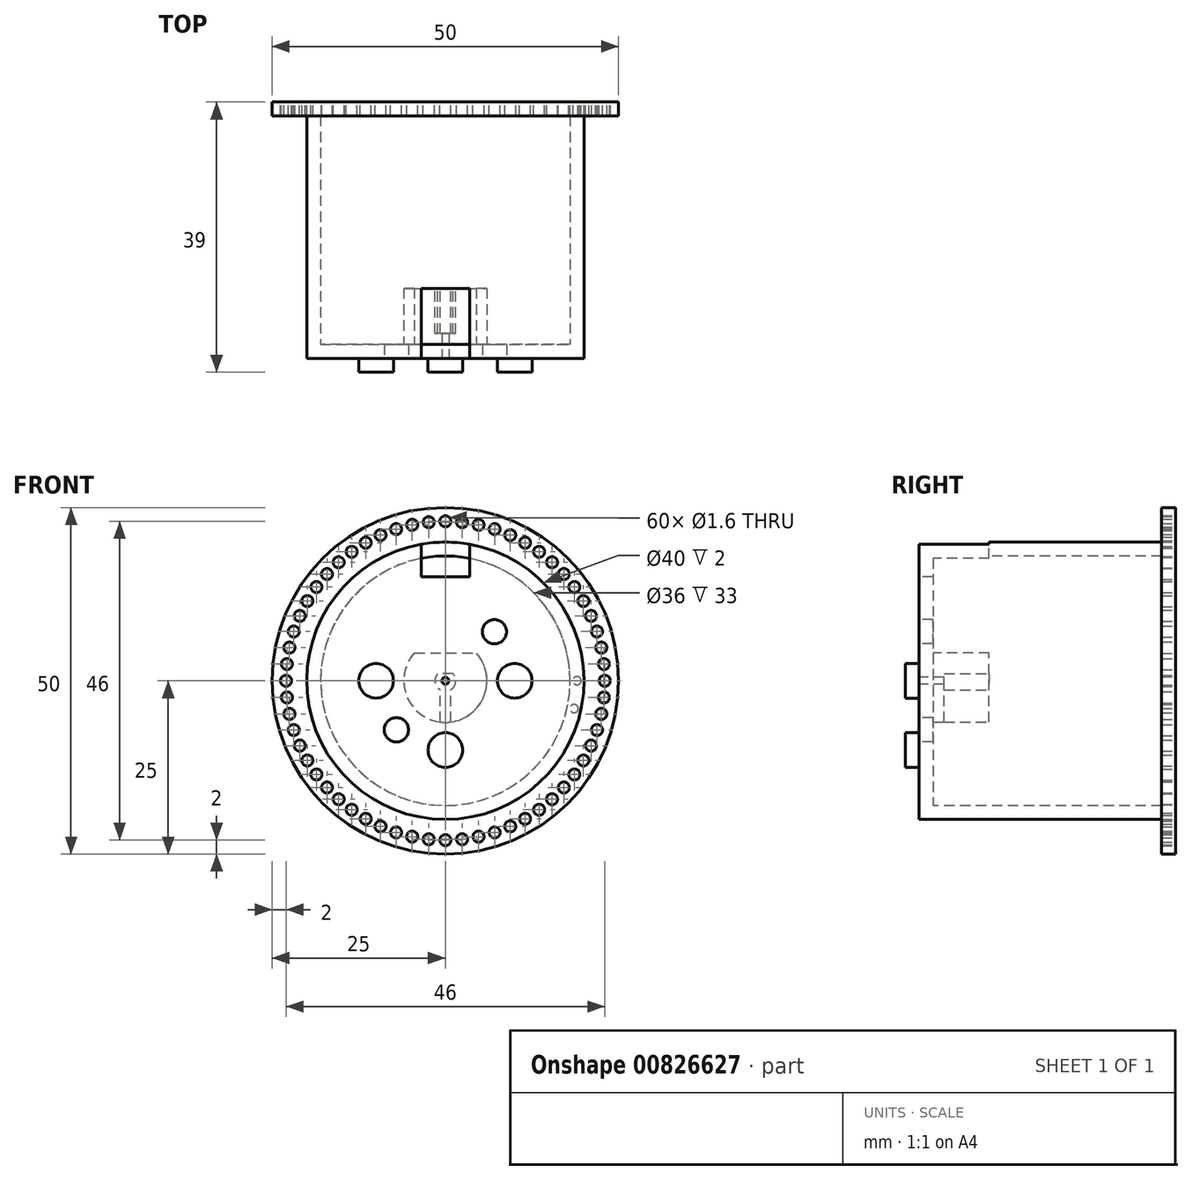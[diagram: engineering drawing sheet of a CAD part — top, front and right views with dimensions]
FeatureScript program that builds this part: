
annotation { "Feature Type Name" : "Feature", "Feature Type Description" : "" }
export const myFeature = defineFeature(function(context is Context, id is Id, definition is map)
    precondition{}
    {
        {
            var Q0;
            Q0=qCreatedBy(makeId("Front.planeOp"),FACE);
            var sketch = newSketch(context, id + "F0", { "sketchPlane" : qUnion([Q0])});
            skCircle(sketch, "E0", {"center": v(0, 0) * mm, "radius": 20 * mm});
            skCircle(sketch, "E1", {"center": v(0, 0) * mm, "radius": 6 * mm});
            skLineSegment(sketch, "E2", {"start": v(0, 0) * mm, "end": v(0, 20) * mm, "construction": true});
            skLineSegment(sketch, "E3.bottom", {"start": v(-3.5, 20) * mm, "end": v(3.5, 20) * mm});
            skLineSegment(sketch, "E3.top", {"start": v(-3.5, 15) * mm, "end": v(3.5, 15) * mm});
            skLineSegment(sketch, "E3.left", {"start": v(-3.5, 20) * mm, "end": v(-3.5, 15) * mm});
            skLineSegment(sketch, "E3.right", {"start": v(3.5, 20) * mm, "end": v(3.5, 15) * mm});
            skPoint(sketch, "E4", {"position": v(0, 15) * mm});
            skLineSegment(sketch, "E5", {"start": v(0, -20) * mm, "end": v(0, 0) * mm, "construction": true});
            skLineSegment(sketch, "E6", {"start": v(0, 0) * mm, "end": v(-20, 0) * mm, "construction": true});
            skLineSegment(sketch, "E7", {"start": v(0, 0) * mm, "end": v(20, 0) * mm, "construction": true});
            skPoint(sketch, "E8", {"position": v(-10, 0) * mm});
            skPoint(sketch, "E9", {"position": v(0, -10) * mm});
            skPoint(sketch, "E10", {"position": v(10, 0) * mm});
            skPoint(sketch, "E11", {"position": v(0, 10) * mm});
            skCircle(sketch, "E12", {"center": v(-10, 0) * mm, "radius": 2.5 * mm});
            skCircle(sketch, "E13", {"center": v(10, 0) * mm, "radius": 2.5 * mm});
            skCircle(sketch, "E14", {"center": v(0, -10) * mm, "radius": 2.5 * mm});
            skLineSegment(sketch, "E15", {"start": v(0, 0) * mm, "end": v(-20, -20) * mm, "construction": true});
            skLineSegment(sketch, "E16", {"start": v(0, 0) * mm, "end": v(20, 20) * mm, "construction": true});
            skLineSegment(sketch, "E17", {"start": v(0, 0) * mm, "end": v(20, -20) * mm, "construction": true});
            skLineSegment(sketch, "E18", {"start": v(0, 0) * mm, "end": v(-14.14, -14.14) * mm, "construction": true});
            skCircle(sketch, "E19", {"center": v(-7.07, -7.07) * mm, "radius": 1.75 * mm});
            skLineSegment(sketch, "E20", {"start": v(0, 0) * mm, "end": v(14.14, 14.14) * mm, "construction": true});
            skCircle(sketch, "E21", {"center": v(7.07, 7.07) * mm, "radius": 1.75 * mm});
            skLineSegment(sketch, "E22", {"start": v(-4.47, 4) * mm, "end": v(4.47, 4) * mm});
            skCircle(sketch, "E23", {"center": v(0, 0) * mm, "radius": 0.5 * mm});
            skSolve(sketch);
        }
        {
            var Q0;
            Q0=makeQuery(id+"F0.imprint","IMPRINT",FACE,{"disambiguationData":[TD([[makeQuery(id+"F0.imprint","IMPRINT",EDGE,{"derivedFrom":sQuery(id+"F0.wireOp",EDGE,"E1")}),-1.0]])]});
            var Q1;
            Q1=makeQuery(id+"F0.imprint","IMPRINT",FACE,{"disambiguationData":[TD([[makeQuery(id+"F0.imprint","IMPRINT",EDGE,{"derivedFrom":sQuery(id+"F0.wireOp",EDGE,"E1")}),1.0]])]});
            var Q2;
            {var subQ1=sQuery(id+"F0.wireOp",EDGE,"E3.top");Q2=makeQuery(id+"F0.imprint","IMPRINT",FACE,{"disambiguationData":[TD([[makeQuery(id+"F0.imprint","IMPRINT",EDGE,{"derivedFrom":subQ1}),1.0]])]});}
            var Q3;
            {var subQ0=sQuery(id+"F0.wireOp",EDGE,"Ytkhx9iy-BOv9-2ljm-Vuet-2ZozW4X65qVo.right");Q3=makeQuery(id+"F0.imprint","IMPRINT",FACE,{"disambiguationData":[TD([[makeQuery(id+"F0.imprint","IMPRINT",EDGE,{"derivedFrom":subQ0}),-1.0]])]});}
            var Q4;
            {var subQ0=sQuery(id+"F0.wireOp",EDGE,"KaZ6fn21-f6RE-yPpd-ZOH6-FnEf13cd3E14.left");Q4=makeQuery(id+"F0.imprint","IMPRINT",FACE,{"disambiguationData":[TD([[makeQuery(id+"F0.imprint","IMPRINT",EDGE,{"derivedFrom":subQ0}),1.0]])]});}
            var Q5;
            {var subQ1=sQuery(id+"F0.wireOp",EDGE,"QGJammbx-tseF-7Ff8-FYSq-d8eIJjrRkEd8.bottom");Q5=makeQuery(id+"F0.imprint","IMPRINT",FACE,{"disambiguationData":[TD([[makeQuery(id+"F0.imprint","IMPRINT",EDGE,{"derivedFrom":subQ1}),-1.0]])]});}
            var Q6;
            Q6=makeQuery(id+"F0.imprint","IMPRINT",FACE,{"disambiguationData":[TD([[makeQuery(id+"F0.imprint","IMPRINT",EDGE,{"derivedFrom":sQuery(id+"F0.wireOp",EDGE,"E12")}),1.0]])]});
            var Q7;
            Q7=makeQuery(id+"F0.imprint","IMPRINT",FACE,{"disambiguationData":[TD([[makeQuery(id+"F0.imprint","IMPRINT",EDGE,{"derivedFrom":sQuery(id+"F0.wireOp",EDGE,"E19")}),1.0]])]});
            var Q8;
            Q8=makeQuery(id+"F0.imprint","IMPRINT",FACE,{"disambiguationData":[TD([[makeQuery(id+"F0.imprint","IMPRINT",EDGE,{"derivedFrom":sQuery(id+"F0.wireOp",EDGE,"E14")}),1.0]])]});
            var Q9;
            Q9=makeQuery(id+"F0.imprint","IMPRINT",FACE,{"disambiguationData":[TD([[makeQuery(id+"F0.imprint","IMPRINT",EDGE,{"derivedFrom":sQuery(id+"F0.wireOp",EDGE,"E13")}),1.0]])]});
            var Q10;
            Q10=makeQuery(id+"F0.imprint","IMPRINT",FACE,{"disambiguationData":[TD([[makeQuery(id+"F0.imprint","IMPRINT",EDGE,{"derivedFrom":sQuery(id+"F0.wireOp",EDGE,"E21")}),1.0]])]});
            var Q11;
            {var subQ0=sQuery(id+"F0.wireOp",EDGE,"E22");Q11=makeQuery(id+"F0.imprint","IMPRINT",FACE,{"disambiguationData":[TD([[makeQuery(id+"F0.imprint","IMPRINT",EDGE,{"derivedFrom":subQ0}),-1.0]])]});}
            var Q12;
            Q12=makeQuery(id+"F0.imprint","IMPRINT",FACE,{"disambiguationData":[TD([[makeQuery(id+"F0.imprint","IMPRINT",EDGE,{"derivedFrom":sQuery(id+"F0.wireOp",EDGE,"E23")}),1.0]])]});
            extrude(context, id + "F1", {"entities" : qUnion([Q0, Q1, Q2, Q3, Q4, Q5, Q6, Q7, Q8, Q9, Q10, Q11, Q12]), "oppositeDirection" : true, "depth" : 37 * mm});
        }
        {
            var Q0;
            Q0=makeQuery(id+"F1.opExtrude","CAP_FACE",FACE,{"disambiguationData":[OSD([sQuery(id+"F0.wireOp",EDGE,"E0"),sQuery(id+"F0.wireOp",EDGE,"E3.top"),sQuery(id+"F0.wireOp",EDGE,"E3.left"),sQuery(id+"F0.wireOp",EDGE,"E3.right")])],"isStart":false});
            var Q1;
            Q1=makeQuery(id+"F1.opExtrude","SWEPT_FACE",FACE,{"disambiguationData":[OSD([sQuery(id+"F0.wireOp",EDGE,"E19")])]});
            var Q2;
            Q2=makeQuery(id+"F1.opExtrude","SWEPT_FACE",FACE,{"disambiguationData":[OSD([sQuery(id+"F0.wireOp",EDGE,"E14")])]});
            var Q3;
            Q3=makeQuery(id+"F1.opExtrude","SWEPT_FACE",FACE,{"disambiguationData":[OSD([sQuery(id+"F0.wireOp",EDGE,"E21")])]});
            var Q4;
            Q4=makeQuery(id+"F1.opExtrude","SWEPT_FACE",FACE,{"disambiguationData":[OSD([sQuery(id+"F0.wireOp",EDGE,"E13")])]});
            var Q5;
            Q5=makeQuery(id+"F1.opExtrude","SWEPT_FACE",FACE,{"disambiguationData":[OSD([sQuery(id+"F0.wireOp",EDGE,"E12")])]});
            shell(context, id + "F2", {"entities" : qUnion([Q0, Q1, Q2, Q3, Q4, Q5]), "thickness" : 2 * mm});
        }
        {
            var Q0;
            Q0=makeQuery(id+"F1.opExtrude","CAP_FACE",FACE,{"disambiguationData":[OSD([sQuery(id+"F0.wireOp",EDGE,"E0")])],"isStart":false});
            var sketch = newSketch(context, id + "F3", { "sketchPlane" : qUnion([Q0])});
            skCircle(sketch, "E24", {"center": v(0, 0) * mm, "radius": 25 * mm});
            skCircle(sketch, "E25", {"center": v(-23, 0) * mm, "radius": 0.8 * mm});
            skCircle(sketch, "E26.1.0", {"center": v(-22.87, -2.4) * mm, "radius": 0.8 * mm});
            skCircle(sketch, "E26.2.0", {"center": v(-22.5, -4.78) * mm, "radius": 0.8 * mm});
            skCircle(sketch, "E26.3.0", {"center": v(-21.87, -7.1) * mm, "radius": 0.8 * mm});
            skCircle(sketch, "E26.4.0", {"center": v(-21.01, -9.35) * mm, "radius": 0.8 * mm});
            skCircle(sketch, "E26.5.0", {"center": v(-19.92, -11.5) * mm, "radius": 0.8 * mm});
            skCircle(sketch, "E26.6.0", {"center": v(-18.6, -13.52) * mm, "radius": 0.8 * mm});
            skCircle(sketch, "E26.7.0", {"center": v(-17.1, -15.4) * mm, "radius": 0.8 * mm});
            skCircle(sketch, "E26.8.0", {"center": v(-15.4, -17.1) * mm, "radius": 0.8 * mm});
            skCircle(sketch, "E26.9.0", {"center": v(-13.52, -18.6) * mm, "radius": 0.8 * mm});
            skCircle(sketch, "E26.10.0", {"center": v(-11.5, -19.92) * mm, "radius": 0.8 * mm});
            skCircle(sketch, "E26.11.0", {"center": v(-9.35, -21.01) * mm, "radius": 0.8 * mm});
            skCircle(sketch, "E26.12.0", {"center": v(-7.1, -21.87) * mm, "radius": 0.8 * mm});
            skCircle(sketch, "E26.13.0", {"center": v(-4.78, -22.5) * mm, "radius": 0.8 * mm});
            skCircle(sketch, "E26.14.0", {"center": v(-2.4, -22.87) * mm, "radius": 0.8 * mm});
            skCircle(sketch, "E26.15.0", {"center": v(0, -23) * mm, "radius": 0.8 * mm});
            skCircle(sketch, "E26.16.0", {"center": v(2.4, -22.87) * mm, "radius": 0.8 * mm});
            skCircle(sketch, "E26.17.0", {"center": v(4.78, -22.5) * mm, "radius": 0.8 * mm});
            skCircle(sketch, "E26.18.0", {"center": v(7.1, -21.87) * mm, "radius": 0.8 * mm});
            skCircle(sketch, "E26.19.0", {"center": v(9.35, -21.01) * mm, "radius": 0.8 * mm});
            skCircle(sketch, "E26.20.0", {"center": v(11.5, -19.92) * mm, "radius": 0.8 * mm});
            skCircle(sketch, "E26.21.0", {"center": v(13.52, -18.6) * mm, "radius": 0.8 * mm});
            skCircle(sketch, "E26.22.0", {"center": v(15.4, -17.1) * mm, "radius": 0.8 * mm});
            skCircle(sketch, "E26.23.0", {"center": v(17.1, -15.4) * mm, "radius": 0.8 * mm});
            skCircle(sketch, "E26.24.0", {"center": v(18.6, -13.52) * mm, "radius": 0.8 * mm});
            skCircle(sketch, "E26.25.0", {"center": v(19.92, -11.5) * mm, "radius": 0.8 * mm});
            skCircle(sketch, "E27.1.26.0", {"center": v(21.01, -9.35) * mm, "radius": 0.8 * mm});
            skCircle(sketch, "E27.1.27.0", {"center": v(21.87, -7.1) * mm, "radius": 0.8 * mm});
            skCircle(sketch, "E27.1.28.0", {"center": v(22.5, -4.78) * mm, "radius": 0.8 * mm});
            skCircle(sketch, "E27.1.29.0", {"center": v(22.87, -2.4) * mm, "radius": 0.8 * mm});
            skCircle(sketch, "E27.1.30.0", {"center": v(23, 0) * mm, "radius": 0.8 * mm});
            skCircle(sketch, "E27.1.31.0", {"center": v(22.87, 2.4) * mm, "radius": 0.8 * mm});
            skCircle(sketch, "E27.1.32.0", {"center": v(22.5, 4.78) * mm, "radius": 0.8 * mm});
            skCircle(sketch, "E27.1.33.0", {"center": v(21.87, 7.1) * mm, "radius": 0.8 * mm});
            skCircle(sketch, "E27.1.34.0", {"center": v(21.01, 9.35) * mm, "radius": 0.8 * mm});
            skCircle(sketch, "E27.1.35.0", {"center": v(19.92, 11.5) * mm, "radius": 0.8 * mm});
            skCircle(sketch, "E28", {"center": v(-19, 0) * mm, "radius": 0.6 * mm});
            skLineSegment(sketch, "E29", {"start": v(0, -20) * mm, "end": v(0, 20) * mm, "construction": true});
            skCircle(sketch, "E30", {"center": v(-31.42, 9.46) * mm, "radius": 0.75 * mm});
            skLineSegment(sketch, "E31", {"start": v(0, 0) * mm, "end": v(22.5, 2.4) * mm, "construction": true});
            skCircle(sketch, "E32.MirrorC", {"center": v(-18.57, -4.01) * mm, "radius": 0.6 * mm});
            skCircle(sketch, "E33.1.36.0", {"center": v(18.6, 13.52) * mm, "radius": 0.8 * mm});
            skCircle(sketch, "E33.1.37.0", {"center": v(17.1, 15.4) * mm, "radius": 0.8 * mm});
            skCircle(sketch, "E33.1.38.0", {"center": v(15.4, 17.1) * mm, "radius": 0.8 * mm});
            skCircle(sketch, "E33.1.39.0", {"center": v(13.52, 18.6) * mm, "radius": 0.8 * mm});
            skCircle(sketch, "E33.1.40.0", {"center": v(11.5, 19.92) * mm, "radius": 0.8 * mm});
            skCircle(sketch, "E33.1.41.0", {"center": v(9.35, 21.01) * mm, "radius": 0.8 * mm});
            skCircle(sketch, "E33.1.42.0", {"center": v(7.1, 21.87) * mm, "radius": 0.8 * mm});
            skCircle(sketch, "E33.1.43.0", {"center": v(4.78, 22.5) * mm, "radius": 0.8 * mm});
            skCircle(sketch, "E33.1.44.0", {"center": v(2.4, 22.87) * mm, "radius": 0.8 * mm});
            skCircle(sketch, "E33.1.45.0", {"center": v(0, 23) * mm, "radius": 0.8 * mm});
            skCircle(sketch, "E33.1.46.0", {"center": v(-2.4, 22.87) * mm, "radius": 0.8 * mm});
            skCircle(sketch, "E33.1.47.0", {"center": v(-4.78, 22.5) * mm, "radius": 0.8 * mm});
            skCircle(sketch, "E33.1.48.0", {"center": v(-7.1, 21.87) * mm, "radius": 0.8 * mm});
            skCircle(sketch, "E33.1.49.0", {"center": v(-9.35, 21.01) * mm, "radius": 0.8 * mm});
            skCircle(sketch, "E33.1.50.0", {"center": v(-11.5, 19.92) * mm, "radius": 0.8 * mm});
            skCircle(sketch, "E33.1.51.0", {"center": v(-13.52, 18.6) * mm, "radius": 0.8 * mm});
            skCircle(sketch, "E33.1.52.0", {"center": v(-15.4, 17.1) * mm, "radius": 0.8 * mm});
            skCircle(sketch, "E33.1.53.0", {"center": v(-17.1, 15.4) * mm, "radius": 0.8 * mm});
            skCircle(sketch, "E33.1.54.0", {"center": v(-18.6, 13.52) * mm, "radius": 0.8 * mm});
            skCircle(sketch, "E33.1.55.0", {"center": v(-19.92, 11.5) * mm, "radius": 0.8 * mm});
            skCircle(sketch, "E33.1.56.0", {"center": v(-21.01, 9.35) * mm, "radius": 0.8 * mm});
            skCircle(sketch, "E33.1.57.0", {"center": v(-21.87, 7.1) * mm, "radius": 0.8 * mm});
            skCircle(sketch, "E33.1.58.0", {"center": v(-22.5, 4.78) * mm, "radius": 0.8 * mm});
            skCircle(sketch, "E33.1.59.0", {"center": v(-22.87, 2.4) * mm, "radius": 0.8 * mm});
            skSolve(sketch);
        }
        {
            var Q0;
            Q0=makeQuery(id+"F3.imprint","IMPRINT",FACE,{"disambiguationData":[TD([[makeQuery(id+"F3.imprint","IMPRINT",EDGE,{"derivedFrom":sQuery(id+"F3.wireOp",EDGE,"E24")}),1.0]])]});
            extrude(context, id + "F4", {"entities" : qUnion([Q0]), "operationType" : NewBodyOperationType.ADD, "oppositeDirection" : true, "depth" : 2 * mm});
        }
        {
            var Q0;
            Q0=makeQuery(id+"F3.imprint","IMPRINT",FACE,{"disambiguationData":[TD([[makeQuery(id+"F3.imprint","IMPRINT",EDGE,{"derivedFrom":sQuery(id+"F3.wireOp",EDGE,"E28")}),1.0]])]});
            var Q1;
            Q1=makeQuery(id+"F3.imprint","IMPRINT",FACE,{"disambiguationData":[TD([[makeQuery(id+"F3.imprint","IMPRINT",EDGE,{"derivedFrom":sQuery(id+"F3.wireOp",EDGE,"E32.MirrorC")}),-1.0]])]});
            extrude(context, id + "F5", {"entities" : qUnion([Q0, Q1]), "operationType" : NewBodyOperationType.REMOVE, "oppositeDirection" : true, "depth" : 2 * mm});
        }
        {
            var Q0;
            {var subQ0=sQuery(id+"F0.wireOp",EDGE,"E22");Q0=makeQuery(id+"F0.imprint","IMPRINT",FACE,{"disambiguationData":[TD([[makeQuery(id+"F0.imprint","IMPRINT",EDGE,{"derivedFrom":subQ0}),-1.0]])]});}
            extrude(context, id + "F6", {"entities" : qUnion([Q0]), "operationType" : NewBodyOperationType.ADD, "oppositeDirection" : true, "depth" : 10.1 * mm});
        }
        {
            var Q0;
            {var subQ1=sQuery(id+"F0.wireOp",EDGE,"E3.top");Q0=makeQuery(id+"F0.imprint","IMPRINT",FACE,{"disambiguationData":[TD([[makeQuery(id+"F0.imprint","IMPRINT",EDGE,{"derivedFrom":subQ1}),1.0]])]});}
            var Q1;
            Q1=makeQuery(id+"F6.opExtrude","CAP_FACE",FACE,{"disambiguationData":[OSD([sQuery(id+"F0.wireOp",EDGE,"E1")])],"isStart":false});
            extrude(context, id + "F7", {"entities" : qUnion([Q0]), "operationType" : NewBodyOperationType.REMOVE, "endBound" : BoundingType.UP_TO_SURFACE, "oppositeDirection" : true, "endBoundEntityFace" : qUnion([Q1]), "depth" : 10 * mm});
        }
        {
            var Q0;
            Q0=makeQuery(id+"F6.opExtrude","CAP_FACE",FACE,{"disambiguationData":[OSD([sQuery(id+"F0.wireOp",EDGE,"E1")])],"isStart":false});
            var sketch = newSketch(context, id + "F8", { "sketchPlane" : qUnion([Q0])});
            skArc(sketch, "E34", {"start": v(-1.12, 1) * mm, "mid": v(0, -1.5) * mm, "end": v(1.12, 1) * mm});
            skLineSegment(sketch, "E35", {"start": v(-1.12, 1) * mm, "end": v(1.12, 1) * mm});
            skLineSegment(sketch, "E36", {"start": v(-4.47, 4) * mm, "end": v(4.47, 4) * mm});
            skLineSegment(sketch, "E37.bottom", {"start": v(-0.75, -6) * mm, "end": v(0.75, -6) * mm});
            skLineSegment(sketch, "E37.top", {"start": v(-0.75, 0) * mm, "end": v(0.75, 0) * mm});
            skLineSegment(sketch, "E37.left", {"start": v(-0.75, -6) * mm, "end": v(-0.75, 0) * mm});
            skLineSegment(sketch, "E37.right", {"start": v(0.75, -6) * mm, "end": v(0.75, 0) * mm});
            skPoint(sketch, "E38", {"position": v(0, -6) * mm});
            skSolve(sketch);
        }
        {
            var Q0;
            Q0=makeQuery(id+"F8.imprint","IMPRINT",FACE,{"disambiguationData":[TD([[makeQuery(id+"F8.imprint","IMPRINT",EDGE,{"derivedFrom":sQuery(id+"F8.wireOp",EDGE,"E34")}),1.0]])]});
            var Q1;
            {var subQ0=sQuery(id+"F8.wireOp",EDGE,"E37.left");var subQ3=sQuery(id+"F8.wireOp",EDGE,"E34");var subQ4=makeQuery(id+"F8.imprint","INTERSECT",VERTEX,{"derivedFrom":[subQ3,subQ0]});Q1=makeQuery(id+"F8.imprint","IMPRINT",FACE,{"disambiguationData":[TD([[makeQuery(id+"F8.imprint","IMPRINT",EDGE,{"disambiguationData":[TD([[subQ4,-1.0]])],"derivedFrom":subQ3}),1.0]])]});}
            var Q2;
            {var subQ2=sQuery(id+"F8.wireOp",EDGE,"E37.left");var subQ5=sQuery(id+"F8.wireOp",EDGE,"E34");var subQ8=makeQuery(id+"F8.imprint","INTERSECT",VERTEX,{"derivedFrom":[subQ5,subQ2]});Q2=makeQuery(id+"F8.imprint","IMPRINT",FACE,{"disambiguationData":[TD([[makeQuery(id+"F8.imprint","IMPRINT",EDGE,{"disambiguationData":[TD([[subQ8,-1.0]])],"derivedFrom":subQ5}),-1.0]])]});}
            var Q3;
            {var subQ0=sQuery(id+"F0.wireOp",EDGE,"E0");Q3=makeQuery(id+"FelEgGFwdY7wIB0_0.boolean.opBoolean","MERGE",FACE,{"derivedFrom":[makeQuery(id+"F1.opExtrude","CAP_FACE",FACE,{"disambiguationData":[OSD([subQ0])],"isStart":true}),makeQuery(id+"FelEgGFwdY7wIB0_0.opExtrude","CAP_FACE",FACE,{"disambiguationData":[OSD([subQ0,sQuery(id+"F0.wireOp",EDGE,"1R5r3tbG-fw4S-uLm3-zZHl-8xL3PTXGlcnv"),sQuery(id+"F0.wireOp",EDGE,"Sdw5IeWT-c1RX-m7VR-ipaU-qvMlsCHA44hO"),sQuery(id+"F0.wireOp",EDGE,"fded56d8-0642-4762-9e0a-157306a48c7e.1.0"),sQuery(id+"F0.wireOp",EDGE,"fded56d8-0642-4762-9e0a-157306a48c7e.2.0"),sQuery(id+"F0.wireOp",EDGE,"fded56d8-0642-4762-9e0a-157306a48c7e.3.0"),sQuery(id+"F0.wireOp",EDGE,"fded56d8-0642-4762-9e0a-157306a48c7e.4.0"),sQuery(id+"F0.wireOp",EDGE,"fded56d8-0642-4762-9e0a-157306a48c7e.5.0"),sQuery(id+"F0.wireOp",EDGE,"fded56d8-0642-4762-9e0a-157306a48c7e.6.0"),sQuery(id+"F0.wireOp",EDGE,"fded56d8-0642-4762-9e0a-157306a48c7e.7.0"),sQuery(id+"F0.wireOp",EDGE,"fded56d8-0642-4762-9e0a-157306a48c7e.8.0"),sQuery(id+"F0.wireOp",EDGE,"fded56d8-0642-4762-9e0a-157306a48c7e.9.0"),sQuery(id+"F0.wireOp",EDGE,"fded56d8-0642-4762-9e0a-157306a48c7e.10.0"),sQuery(id+"F0.wireOp",EDGE,"fded56d8-0642-4762-9e0a-157306a48c7e.11.0"),sQuery(id+"F0.wireOp",EDGE,"fded56d8-0642-4762-9e0a-157306a48c7e.12.0"),sQuery(id+"F0.wireOp",EDGE,"fded56d8-0642-4762-9e0a-157306a48c7e.13.0"),sQuery(id+"F0.wireOp",EDGE,"fded56d8-0642-4762-9e0a-157306a48c7e.14.0"),sQuery(id+"F0.wireOp",EDGE,"fded56d8-0642-4762-9e0a-157306a48c7e.15.0"),sQuery(id+"F0.wireOp",EDGE,"fded56d8-0642-4762-9e0a-157306a48c7e.16.0"),sQuery(id+"F0.wireOp",EDGE,"fded56d8-0642-4762-9e0a-157306a48c7e.17.0"),sQuery(id+"F0.wireOp",EDGE,"fded56d8-0642-4762-9e0a-157306a48c7e.18.0"),sQuery(id+"F0.wireOp",EDGE,"fded56d8-0642-4762-9e0a-157306a48c7e.19.0"),sQuery(id+"F0.wireOp",EDGE,"fded56d8-0642-4762-9e0a-157306a48c7e.20.0"),sQuery(id+"F0.wireOp",EDGE,"fded56d8-0642-4762-9e0a-157306a48c7e.21.0"),sQuery(id+"F0.wireOp",EDGE,"fded56d8-0642-4762-9e0a-157306a48c7e.22.0"),sQuery(id+"F0.wireOp",EDGE,"fded56d8-0642-4762-9e0a-157306a48c7e.23.0"),sQuery(id+"F0.wireOp",EDGE,"fded56d8-0642-4762-9e0a-157306a48c7e.24.0"),sQuery(id+"F0.wireOp",EDGE,"fded56d8-0642-4762-9e0a-157306a48c7e.25.0")])],"isStart":true})]});}
            extrude(context, id + "F9", {"entities" : qUnion([Q0, Q1, Q2]), "operationType" : NewBodyOperationType.REMOVE, "oppositeDirection" : true, "endBoundEntityFace" : qUnion([Q3]), "depth" : 6.5 * mm});
        }
        {
            var Q0;
            Q0=makeQuery(id+"F3.imprint","IMPRINT",FACE,{"disambiguationData":[TD([[makeQuery(id+"F3.imprint","IMPRINT",EDGE,{"derivedFrom":sQuery(id+"F3.wireOp",EDGE,"E28")}),1.0]])]});
            extrude(context, id + "F10", {"entities" : qUnion([Q0]), "oppositeDirection" : true, "depth" : 2 * mm});
        }
        {
            var Q0;
            Q0=makeQuery(id+"F0.imprint","IMPRINT",FACE,{"disambiguationData":[TD([[makeQuery(id+"F0.imprint","IMPRINT",EDGE,{"derivedFrom":sQuery(id+"F0.wireOp",EDGE,"E12")}),1.0]])]});
            var Q1;
            Q1=makeQuery(id+"F0.imprint","IMPRINT",FACE,{"disambiguationData":[TD([[makeQuery(id+"F0.imprint","IMPRINT",EDGE,{"derivedFrom":sQuery(id+"F0.wireOp",EDGE,"E14")}),1.0]])]});
            var Q2;
            Q2=makeQuery(id+"F0.imprint","IMPRINT",FACE,{"disambiguationData":[TD([[makeQuery(id+"F0.imprint","IMPRINT",EDGE,{"derivedFrom":sQuery(id+"F0.wireOp",EDGE,"E13")}),1.0]])]});
            extrude(context, id + "F11", {"entities" : qUnion([Q0, Q1, Q2]), "operationType" : NewBodyOperationType.ADD, "depth" : 2 * mm});
        }
        {
            var Q0;
            Q0=makeQuery(id+"F0.imprint","IMPRINT",FACE,{"disambiguationData":[TD([[makeQuery(id+"F0.imprint","IMPRINT",EDGE,{"derivedFrom":sQuery(id+"F0.wireOp",EDGE,"E19")}),1.0]])]});
            var Q1;
            Q1=makeQuery(id+"F0.imprint","IMPRINT",FACE,{"disambiguationData":[TD([[makeQuery(id+"F0.imprint","IMPRINT",EDGE,{"derivedFrom":sQuery(id+"F0.wireOp",EDGE,"E21")}),1.0]])]});
            extrude(context, id + "F12", {"entities" : qUnion([Q0, Q1]), "operationType" : NewBodyOperationType.REMOVE, "endBound" : BoundingType.UP_TO_NEXT, "oppositeDirection" : true, "depth" : 25 * mm});
        }
        {
            var Q0;
            Q0=makeQuery(id+"F0.imprint","IMPRINT",FACE,{"disambiguationData":[TD([[makeQuery(id+"F0.imprint","IMPRINT",EDGE,{"derivedFrom":sQuery(id+"F0.wireOp",EDGE,"E23")}),1.0]])]});
            extrude(context, id + "F13", {"entities" : qUnion([Q0]), "operationType" : NewBodyOperationType.REMOVE, "endBound" : BoundingType.UP_TO_NEXT, "oppositeDirection" : true, "depth" : 25 * mm});
        }
    });
